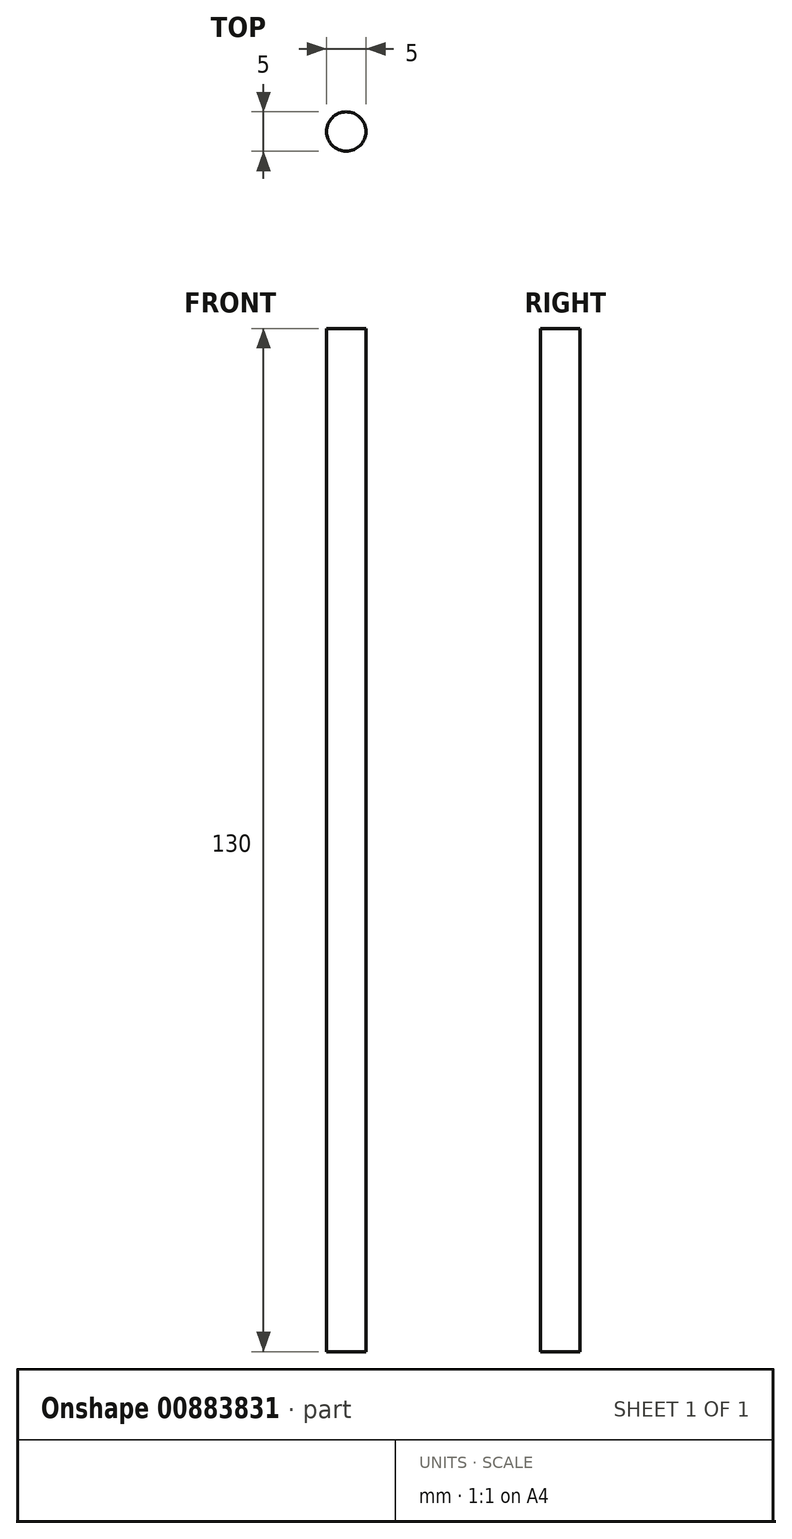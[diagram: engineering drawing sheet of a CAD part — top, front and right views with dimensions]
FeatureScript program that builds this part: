
annotation { "Feature Type Name" : "Feature", "Feature Type Description" : "" }
export const myFeature = defineFeature(function(context is Context, id is Id, definition is map)
    precondition{}
    {
        {
            var Q0;
            Q0=qCreatedBy(makeId("Top.planeOp"),FACE);
            var sketch = newSketch(context, id + "F0", { "sketchPlane" : qUnion([Q0])});
            skCircle(sketch, "E0", {"center": v(-53.9, 31.84) * mm, "radius": 2.5 * mm});
            skSolve(sketch);
        }
        {
            var Q0;
            Q0=makeQuery(id+"F0.imprint","IMPRINT",FACE,{"disambiguationData":[TD([[makeQuery(id+"F0.imprint","IMPRINT",EDGE,{"derivedFrom":sQuery(id+"F0.wireOp",EDGE,"E0")}),1.0]])]});
            extrude(context, id + "F1", {"entities" : qUnion([Q0]), "depth" : 130 * mm, "offsetDistance" : 25 * mm});
        }
    });
